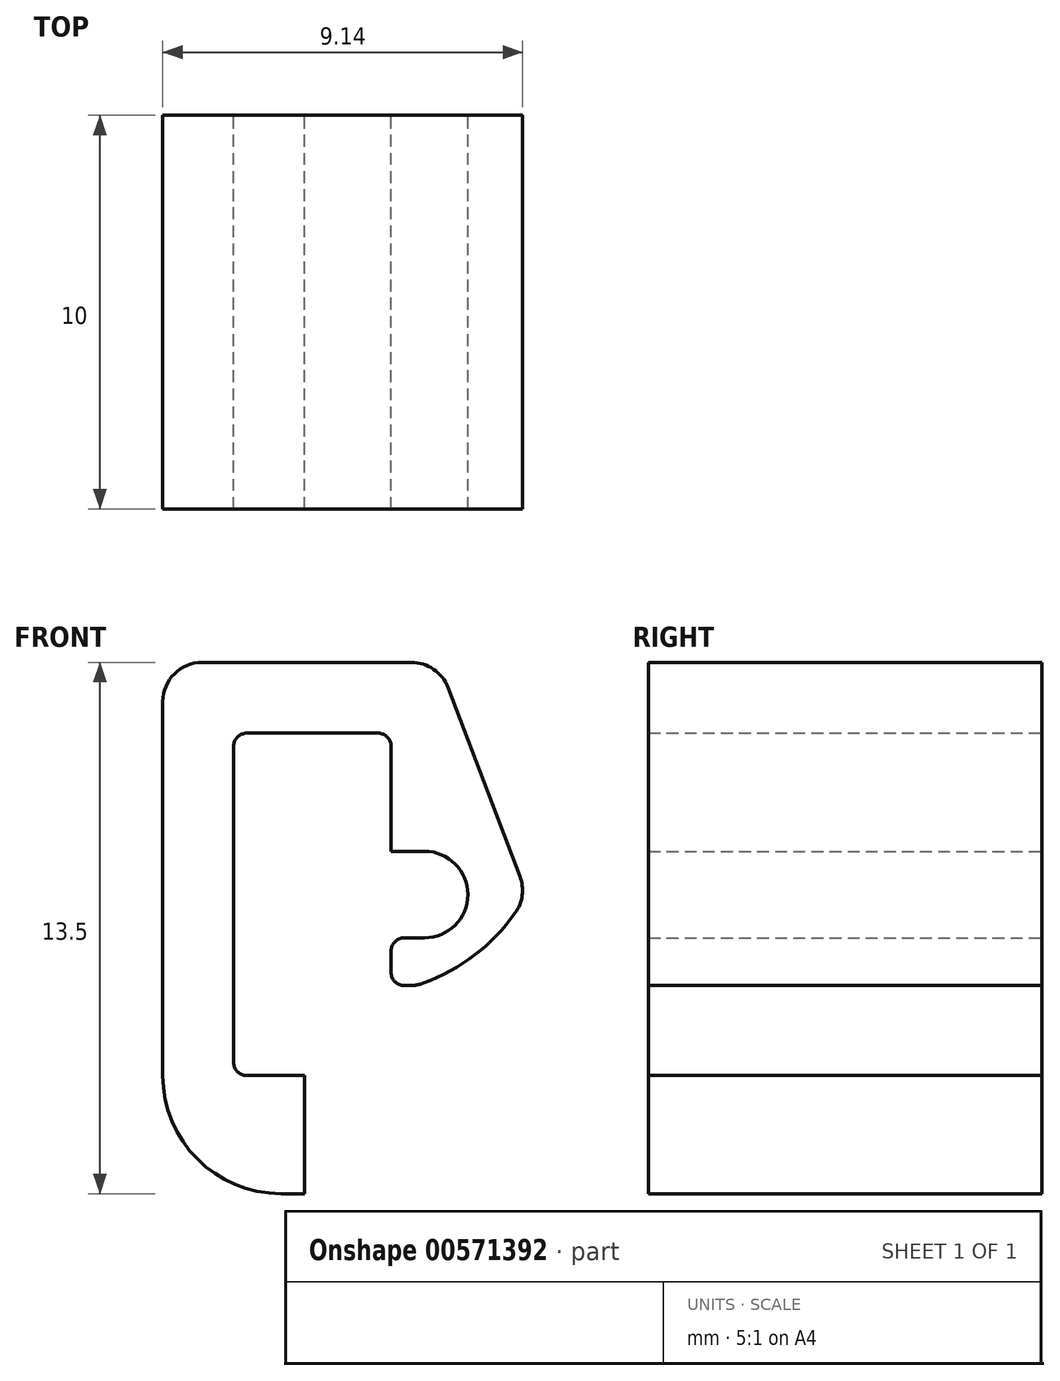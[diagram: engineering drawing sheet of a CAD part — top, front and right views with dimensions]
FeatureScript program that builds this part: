
annotation { "Feature Type Name" : "Feature", "Feature Type Description" : "" }
export const myFeature = defineFeature(function(context is Context, id is Id, definition is map)
    precondition{}
    {
        {
            var Q0;
            Q0=qCreatedBy(makeId("Front.planeOp"),FACE);
            var sketch = newSketch(context, id + "F0", { "sketchPlane" : qUnion([Q0])});
            skLineSegment(sketch, "E0", {"start": v(3.6, 0) * mm, "end": v(0, 0) * mm});
            skLineSegment(sketch, "E1", {"start": v(0, 0) * mm, "end": v(0, 13.5) * mm});
            skLineSegment(sketch, "E2", {"start": v(0, 13.5) * mm, "end": v(7, 13.5) * mm});
            skLineSegment(sketch, "E3", {"start": v(3.6, 0) * mm, "end": v(3.6, 3) * mm});
            skLineSegment(sketch, "E4", {"start": v(3.6, 3) * mm, "end": v(1.8, 3) * mm});
            skLineSegment(sketch, "E5", {"start": v(1.8, 3) * mm, "end": v(1.8, 11.7) * mm});
            skLineSegment(sketch, "E6", {"start": v(1.8, 11.7) * mm, "end": v(5.8, 11.7) * mm});
            skLineSegment(sketch, "E7", {"start": v(6.45, 5.29) * mm, "end": v(5.8, 5.29) * mm});
            skLineSegment(sketch, "E8", {"start": v(5.8, 5.29) * mm, "end": v(5.8, 6.5) * mm});
            skLineSegment(sketch, "E9", {"start": v(5.8, 11.7) * mm, "end": v(5.8, 8.7) * mm});
            skLineSegment(sketch, "E10", {"start": v(5.8, 8.7) * mm, "end": v(6.65, 8.7) * mm});
            skLineSegment(sketch, "E11", {"start": v(5.8, 6.5) * mm, "end": v(6.65, 6.5) * mm});
            skLineSegment(sketch, "E12", {"start": v(9.25, 7.6) * mm, "end": v(7, 13.5) * mm});
            skPoint(sketch, "E13.start.orphan", {"position": v(7.75, 7.6) * mm});
            skPoint(sketch, "E14.center.orphan", {"position": v(5.8, 7.6) * mm});
            skLineSegment(sketch, "E15", {"start": v(7.75, 7.6) * mm, "end": v(9.25, 7.6) * mm});
            skArc(sketch, "E16", {"start": v(6.45, 5.29) * mm, "mid": v(8.07, 6.18) * mm, "end": v(9.25, 7.6) * mm});
            skArc(sketch, "E17", {"start": v(6.65, 6.5) * mm, "mid": v(7.75, 7.6) * mm, "end": v(6.65, 8.7) * mm});
            skSolve(sketch);
        }
        {
            var Q0;
            Q0=makeQuery(id+"F0.imprint","IMPRINT",FACE,{"disambiguationData":[TD([[makeQuery(id+"F0.imprint","IMPRINT",EDGE,{"derivedFrom":sQuery(id+"F0.wireOp",EDGE,"E0")}),-1.0]])]});
            var Q1;
            Q1=makeQuery(id+"F0.imprint","IMPRINT",FACE,{"disambiguationData":[TD([[makeQuery(id+"F0.imprint","IMPRINT",EDGE,{"derivedFrom":sQuery(id+"F0.wireOp",EDGE,"E7")}),-1.0]])]});
            extrude(context, id + "F1", {"entities" : qUnion([Q0, Q1]), "depth" : 10 * mm, "offsetDistance" : 25 * mm});
        }
        {
            var Q0;
            Q0=makeQuery(id+"F1.opExtrude","SWEPT_EDGE",EDGE,{"disambiguationData":[OSD([sQuery(id+"F0.wireOp",EDGE,"E1"),sQuery(id+"F0.wireOp",EDGE,"E2")])]});
            var Q1;
            Q1=makeQuery(id+"F1.opExtrude","SWEPT_EDGE",EDGE,{"disambiguationData":[OSD([sQuery(id+"F0.wireOp",EDGE,"E2"),sQuery(id+"F0.wireOp",EDGE,"E12")])]});
            var Q2;
            Q2=makeQuery(id+"F1.opExtrude","SWEPT_EDGE",EDGE,{"disambiguationData":[OSD([sQuery(id+"F0.wireOp",EDGE,"E12"),sQuery(id+"F0.wireOp",EDGE,"c0oHTTDt-FG6a-EUCl-8E2I-XS0aqP6V1WTL")])]});
            var Q3;
            Q3=makeQuery(id+"F1.opExtrude","SWEPT_EDGE",EDGE,{"disambiguationData":[OSD([sQuery(id+"F0.wireOp",EDGE,"E7"),sQuery(id+"F0.wireOp",EDGE,"E16")])]});
            var Q4;
            Q4=makeQuery(id+"F1.opExtrude","SWEPT_EDGE",EDGE,{"disambiguationData":[OSD([sQuery(id+"F0.wireOp",EDGE,"E12"),sQuery(id+"F0.wireOp",EDGE,"E15"),sQuery(id+"F0.wireOp",EDGE,"E16")])]});
            fillet(context, id + "F2", {"entities" : qUnion([Q0, Q1, Q2, Q3, Q4]), "radius" : 1 * mm, "tangentPropagation" : true, "allowEdgeOverflow" : false});
        }
        {
            var Q0;
            Q0=makeQuery(id+"F1.opExtrude","SWEPT_EDGE",EDGE,{"disambiguationData":[OSD([sQuery(id+"F0.wireOp",EDGE,"E0"),sQuery(id+"F0.wireOp",EDGE,"E1")])]});
            fillet(context, id + "F3", {"entities" : qUnion([Q0]), "radius" : 3 * mm, "tangentPropagation" : true, "allowEdgeOverflow" : false});
        }
        {
            var Q0;
            Q0=makeQuery(id+"F1.opExtrude","SWEPT_EDGE",EDGE,{"disambiguationData":[OSD([sQuery(id+"F0.wireOp",EDGE,"E6"),sQuery(id+"F0.wireOp",EDGE,"E9")])]});
            var Q1;
            Q1=makeQuery(id+"F1.opExtrude","SWEPT_EDGE",EDGE,{"disambiguationData":[OSD([sQuery(id+"F0.wireOp",EDGE,"E7"),sQuery(id+"F0.wireOp",EDGE,"E8")])]});
            var Q2;
            Q2=makeQuery(id+"F1.opExtrude","SWEPT_EDGE",EDGE,{"disambiguationData":[OSD([sQuery(id+"F0.wireOp",EDGE,"E8"),sQuery(id+"F0.wireOp",EDGE,"E11")])]});
            var Q3;
            Q3=makeQuery(id+"F1.opExtrude","SWEPT_EDGE",EDGE,{"disambiguationData":[OSD([sQuery(id+"F0.wireOp",EDGE,"E4"),sQuery(id+"F0.wireOp",EDGE,"E5")])]});
            var Q4;
            Q4=makeQuery(id+"F1.opExtrude","SWEPT_EDGE",EDGE,{"disambiguationData":[OSD([sQuery(id+"F0.wireOp",EDGE,"E5"),sQuery(id+"F0.wireOp",EDGE,"E6")])]});
            fillet(context, id + "F4", {"entities" : qUnion([Q0, Q1, Q2, Q3, Q4]), "radius" : 0.33 * mm, "tangentPropagation" : true, "allowEdgeOverflow" : false});
        }
    });
